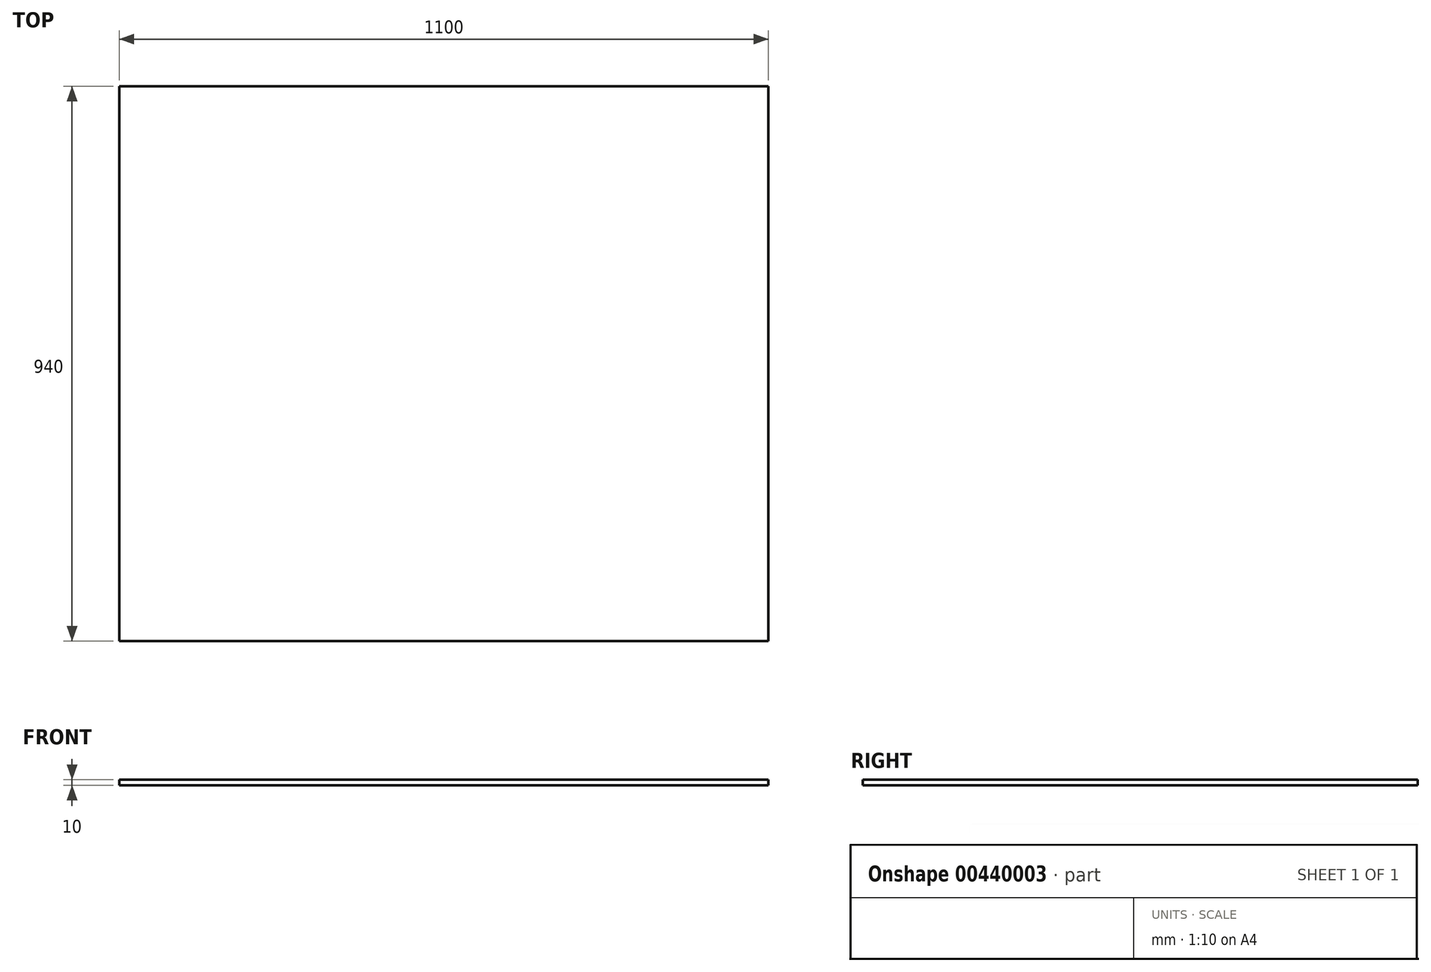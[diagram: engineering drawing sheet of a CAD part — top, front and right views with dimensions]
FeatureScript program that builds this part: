
annotation { "Feature Type Name" : "Feature", "Feature Type Description" : "" }
export const myFeature = defineFeature(function(context is Context, id is Id, definition is map)
    precondition{}
    {
        {
            var Q0;
            Q0=qCreatedBy(makeId("Top.planeOp"),FACE);
            var sketch = newSketch(context, id + "F0", { "sketchPlane" : qUnion([Q0])});
            skLineSegment(sketch, "E0.bottom", {"start": v(-726.2, 459.98) * mm, "end": v(373.8, 459.98) * mm});
            skLineSegment(sketch, "E0.top", {"start": v(-726.2, -480.02) * mm, "end": v(373.8, -480.02) * mm});
            skLineSegment(sketch, "E0.left", {"start": v(-726.2, 459.98) * mm, "end": v(-726.2, -480.02) * mm});
            skLineSegment(sketch, "E0.right", {"start": v(373.8, 459.98) * mm, "end": v(373.8, -480.02) * mm});
            skSolve(sketch);
        }
        {
            var Q0;
            Q0 = qSketchRegion(id + "F0", true);
            extrude(context, id + "F1", {"entities" : qUnion([Q0]), "depth" : 10 * mm});
        }
    });
